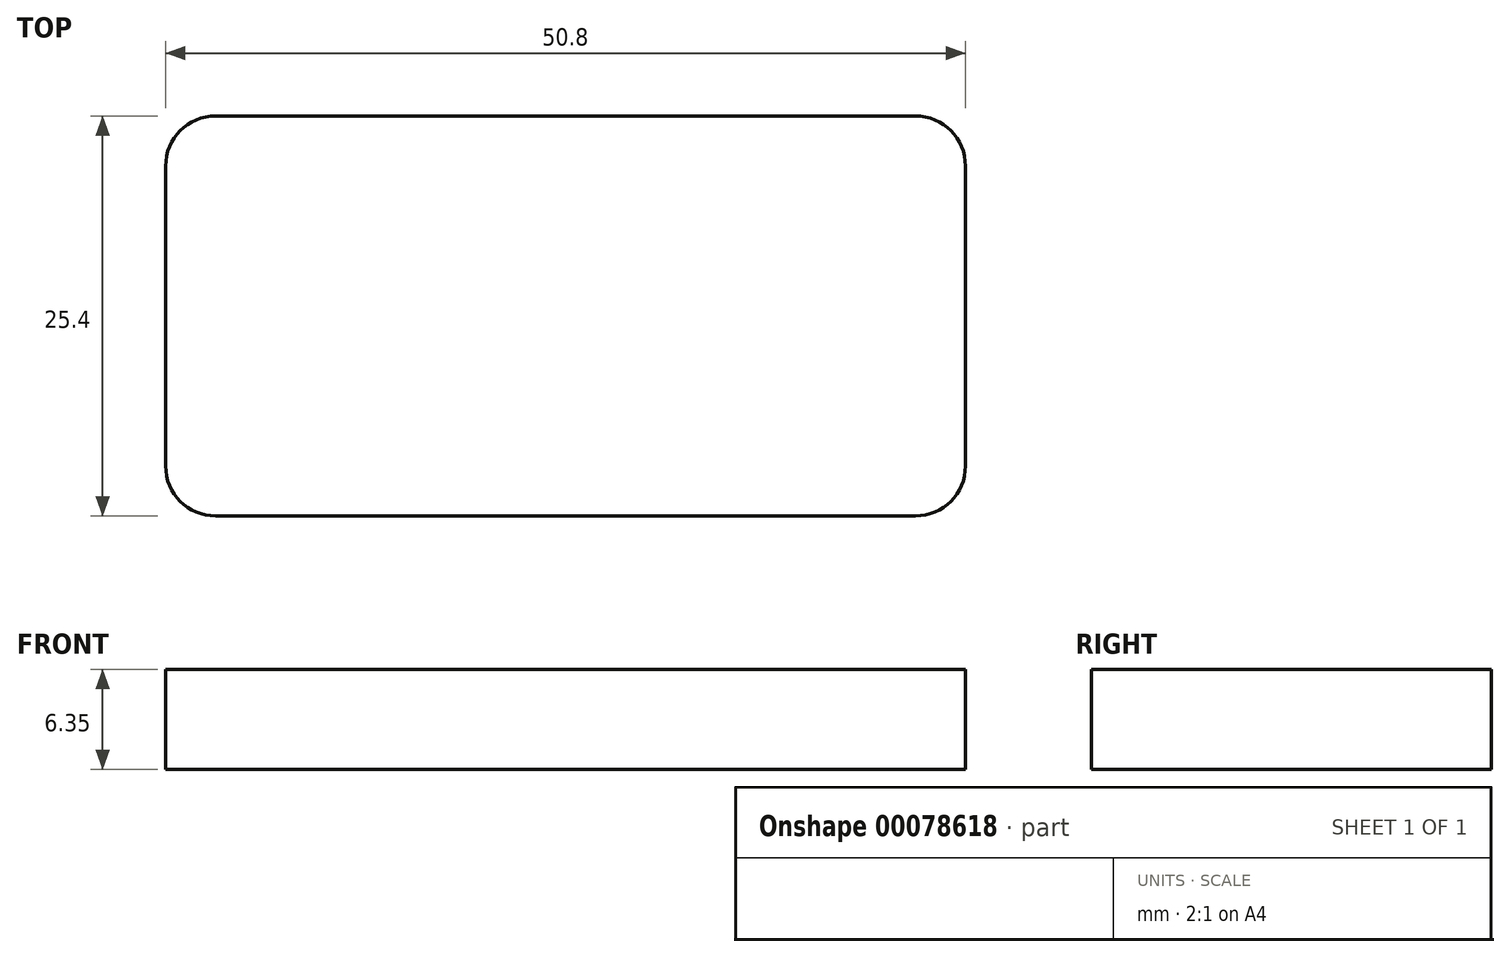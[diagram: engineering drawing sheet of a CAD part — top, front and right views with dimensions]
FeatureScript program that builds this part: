
annotation { "Feature Type Name" : "Feature", "Feature Type Description" : "" }
export const myFeature = defineFeature(function(context is Context, id is Id, definition is map)
    precondition{}
    {
        {
            var Q0;
            Q0=qCreatedBy(makeId("Top.planeOp"),FACE);
            var sketch = newSketch(context, id + "F0", { "sketchPlane" : qUnion([Q0])});
            skLineSegment(sketch, "E0.bottom", {"start": v(0, 0) * mm, "end": v(50.8, 0) * mm});
            skLineSegment(sketch, "E0.top", {"start": v(0, 25.4) * mm, "end": v(50.8, 25.4) * mm});
            skLineSegment(sketch, "E0.left", {"start": v(0, 0) * mm, "end": v(0, 25.4) * mm});
            skLineSegment(sketch, "E0.right", {"start": v(50.8, 0) * mm, "end": v(50.8, 25.4) * mm});
            skSolve(sketch);
        }
        {
            var Q0;
            Q0 = qSketchRegion(id + "F0", true);
            extrude(context, id + "F1", {"entities" : qUnion([Q0]), "depth" : 6.35 * mm});
        }
        {
            var Q0;
            Q0=makeQuery(id+"F1.opExtrude","SWEPT_EDGE",EDGE,{"disambiguationData":[OSD([sQuery(id+"F0.wireOp",EDGE,"E0.bottom"),sQuery(id+"F0.wireOp",EDGE,"E0.right")])]});
            var Q1;
            Q1=makeQuery(id+"F1.opExtrude","SWEPT_EDGE",EDGE,{"disambiguationData":[OSD([sQuery(id+"F0.wireOp",EDGE,"E0.top"),sQuery(id+"F0.wireOp",EDGE,"E0.right")])]});
            var Q2;
            Q2=makeQuery(id+"F1.opExtrude","SWEPT_EDGE",EDGE,{"disambiguationData":[OSD([sQuery(id+"F0.wireOp",EDGE,"E0.bottom"),sQuery(id+"F0.wireOp",EDGE,"E0.left")])]});
            var Q3;
            Q3=makeQuery(id+"F1.opExtrude","SWEPT_EDGE",EDGE,{"disambiguationData":[OSD([sQuery(id+"F0.wireOp",EDGE,"E0.top"),sQuery(id+"F0.wireOp",EDGE,"E0.left")])]});
            fillet(context, id + "F2", {"entities" : qUnion([Q0, Q1, Q2, Q3]), "radius" : 3.17 * mm, "tangentPropagation" : true, "allowEdgeOverflow" : false});
        }
    });
